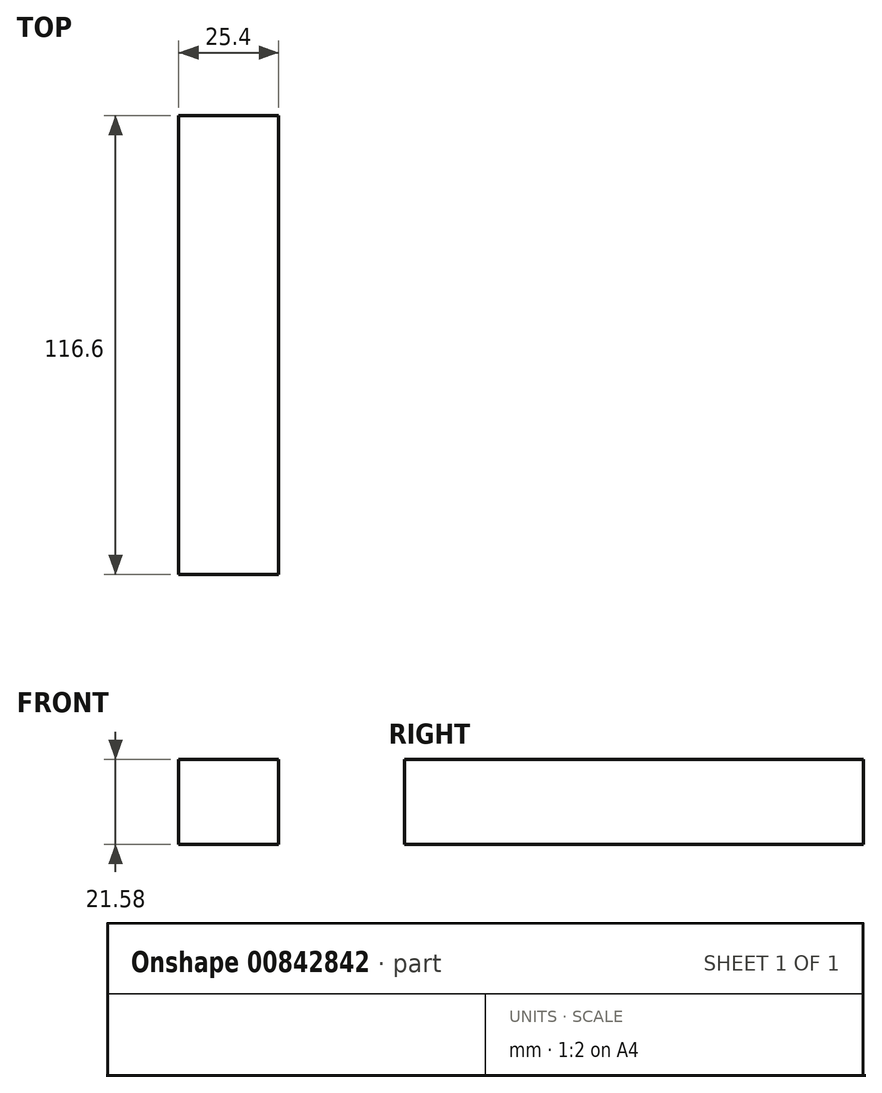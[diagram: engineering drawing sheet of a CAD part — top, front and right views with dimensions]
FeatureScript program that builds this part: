
annotation { "Feature Type Name" : "Feature", "Feature Type Description" : "" }
export const myFeature = defineFeature(function(context is Context, id is Id, definition is map)
    precondition{}
    {
        {
            var Q0;
            Q0=qCreatedBy(makeId("Right.planeOp"),FACE);
            var sketch = newSketch(context, id + "F0", { "sketchPlane" : qUnion([Q0])});
            skLineSegment(sketch, "E0.bottom", {"start": v(58.3, 10.79) * mm, "end": v(-58.3, 10.79) * mm});
            skLineSegment(sketch, "E0.top", {"start": v(58.3, -10.79) * mm, "end": v(-58.3, -10.79) * mm});
            skLineSegment(sketch, "E0.left", {"start": v(58.3, 10.79) * mm, "end": v(58.3, -10.79) * mm});
            skLineSegment(sketch, "E0.right", {"start": v(-58.3, 10.79) * mm, "end": v(-58.3, -10.79) * mm});
            skPoint(sketch, "E0.middle", {"position": v(0, 0) * mm});
            skSolve(sketch);
        }
        {
            var Q0;
            Q0=makeQuery(id+"F0.imprint","IMPRINT",FACE,{"disambiguationData":[TD([[makeQuery(id+"F0.imprint","IMPRINT",EDGE,{"derivedFrom":sQuery(id+"F0.wireOp",EDGE,"E0.bottom")}),1.0]])]});
            extrude(context, id + "F1", {"entities" : qUnion([Q0]), "depth" : 25.4 * mm, "offsetDistance" : 25.4 * mm});
        }
    });
